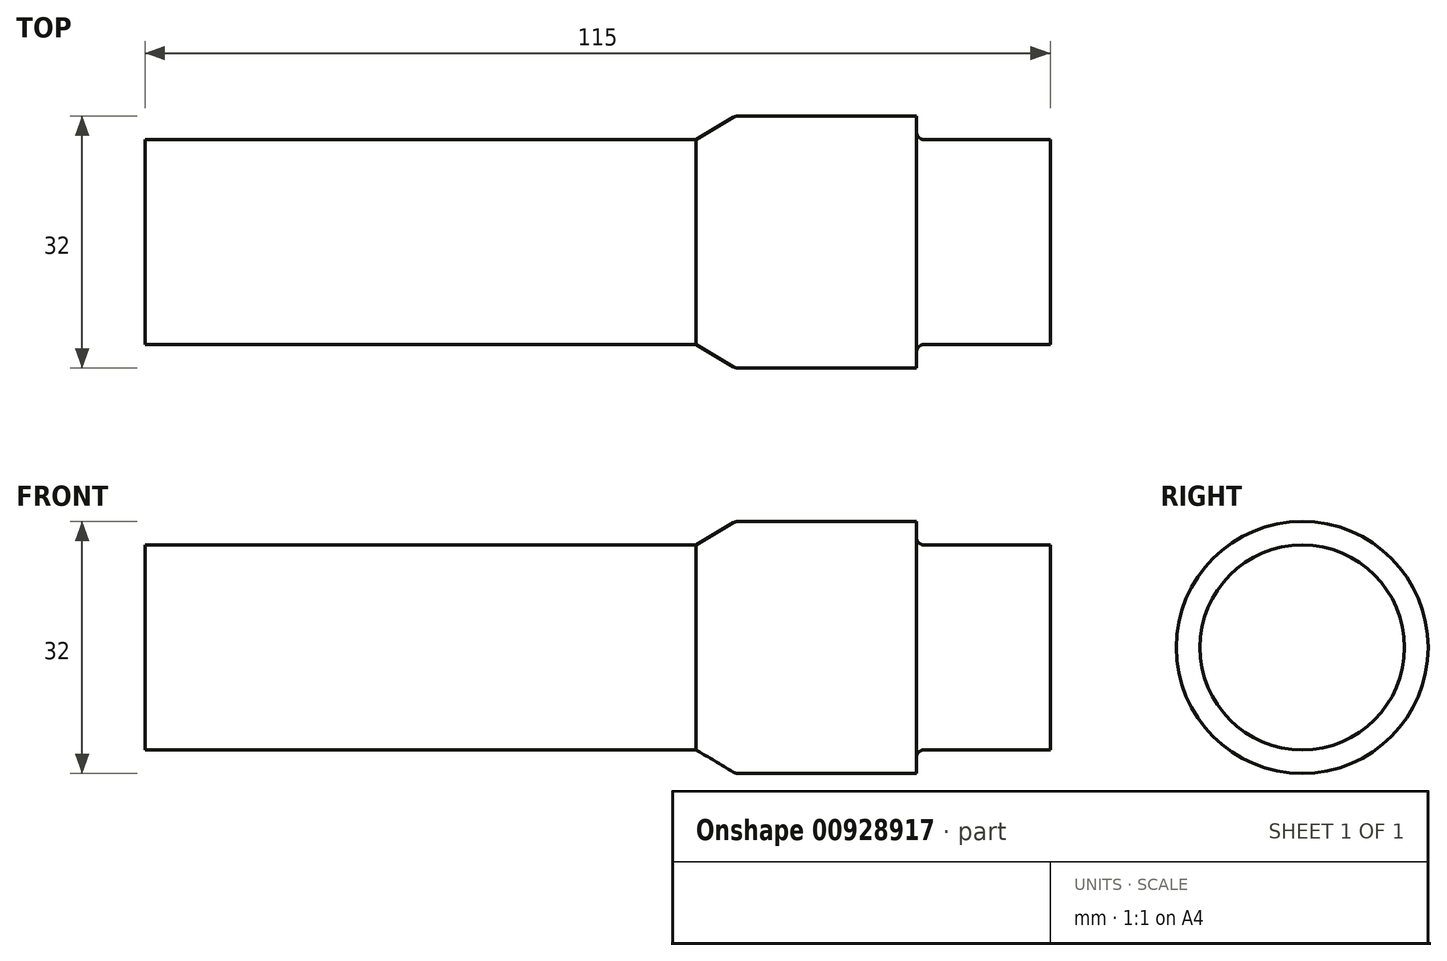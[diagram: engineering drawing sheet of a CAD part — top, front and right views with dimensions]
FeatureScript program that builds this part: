
annotation { "Feature Type Name" : "Feature", "Feature Type Description" : "" }
export const myFeature = defineFeature(function(context is Context, id is Id, definition is map)
    precondition{}
    {
        {
            var Q0;
            Q0=qCreatedBy(makeId("Front.planeOp"),FACE);
            var sketch = newSketch(context, id + "F0", { "sketchPlane" : qUnion([Q0])});
            skLineSegment(sketch, "E0", {"start": v(74.76, 15.86) * mm, "end": v(70, 13) * mm});
            skLineSegment(sketch, "E1", {"start": v(75.28, 16) * mm, "end": v(98, 16) * mm});
            skLineSegment(sketch, "E2", {"start": v(98, 0) * mm, "end": v(70, 0) * mm});
            skPoint(sketch, "E3.visualSharp", {"position": v(75, 16) * mm});
            skArc(sketch, "E3.filletArc", {"start": v(75.28, 16) * mm, "mid": v(75.01, 15.96) * mm, "end": v(74.76, 15.86) * mm});
            skPoint(sketch, "E4.orphan", {"position": v(115, 0) * mm});
            skLineSegment(sketch, "E5", {"start": v(70, 13) * mm, "end": v(0, 13) * mm});
            skLineSegment(sketch, "E6", {"start": v(0, 13) * mm, "end": v(0, 0) * mm});
            skLineSegment(sketch, "E7", {"start": v(0, 0) * mm, "end": v(70, 0) * mm});
            skLineSegment(sketch, "E8", {"start": v(98, 0) * mm, "end": v(115, 0) * mm});
            skLineSegment(sketch, "E9", {"start": v(115, 0) * mm, "end": v(115, 13) * mm});
            skLineSegment(sketch, "E10", {"start": v(115, 13) * mm, "end": v(99, 13) * mm});
            skLineSegment(sketch, "E11", {"start": v(98, 16) * mm, "end": v(98, 14) * mm});
            skPoint(sketch, "E12.visualSharp", {"position": v(98, 13) * mm});
            skArc(sketch, "E12.filletArc", {"start": v(98, 14) * mm, "mid": v(98.3, 13.3) * mm, "end": v(99, 13) * mm});
            skSolve(sketch);
        }
        {
            var Q0;
            Q0 = qSketchRegion(id + "F0", true);
            var Q1;
            Q1=sQuery(id+"F0.wireOp",EDGE,"E2");
            revolve(context, id + "F1", {"surfaceOperationType" : NewSurfaceOperationType.NEW, "entities" : qUnion([Q0]), "axis" : qUnion([Q1]), "revolveType" : RevolveType.FULL});
        }
    });
